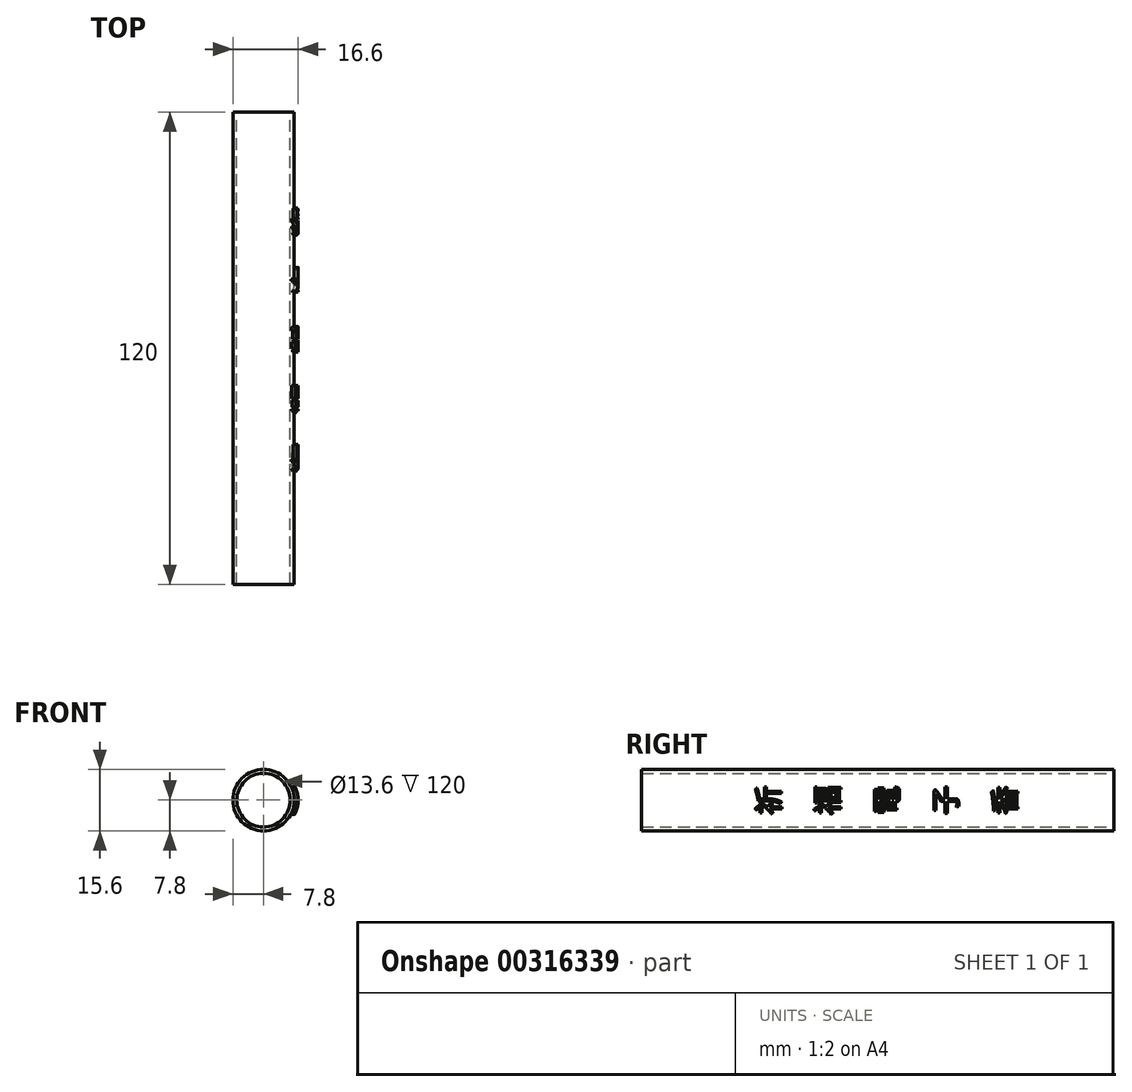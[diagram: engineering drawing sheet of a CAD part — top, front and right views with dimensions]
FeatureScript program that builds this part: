
annotation { "Feature Type Name" : "Feature", "Feature Type Description" : "" }
export const myFeature = defineFeature(function(context is Context, id is Id, definition is map)
    precondition{}
    {
        {
            var Q0;
            Q0=qCreatedBy(makeId("Front.planeOp"),FACE);
            var sketch = newSketch(context, id + "F0", { "sketchPlane" : qUnion([Q0])});
            skCircle(sketch, "E0", {"center": v(0, 0) * mm, "radius": 7.8 * mm});
            skSolve(sketch);
        }
        {
            var Q0;
            Q0=qSketchRegion(id+"F0",true);
            extrude(context, id + "F1", {"entities" : qUnion([Q0]), "depth" : 120 * mm});
        }
        {
            var Q0;
            Q0=makeQuery(id+"F1.opExtrude","CAP_FACE",FACE,{"disambiguationData":[OSD([sQuery(id+"F0.wireOp",EDGE,"E0")])],"isStart":true});
            var sketch = newSketch(context, id + "F2", { "sketchPlane" : qUnion([Q0])});
            skCircle(sketch, "E1", {"center": v(0, 0) * mm, "radius": 6.8 * mm});
            skSolve(sketch);
        }
        {
            var Q0;
            Q0=qSketchRegion(id+"F2",true);
            extrude(context, id + "F3", {"entities" : qUnion([Q0]), "operationType" : NewBodyOperationType.REMOVE, "oppositeDirection" : true, "depth" : 120 * mm});
        }
        {
            var Q0;
            Q0=qCreatedBy(makeId("Right.planeOp"),FACE);
            cPlane(context, id + "F4", {"entities" : qUnion([Q0]), "cplaneType" : CPlaneType.OFFSET, "offset" : 10 * mm, "width" : 150 * mm, "height" : 150 * mm});
        }
        {
            var Q0;
            Q0=qCreatedBy(id+"F4.planeOp",FACE);
            var sketch = newSketch(context, id + "F5", { "sketchPlane" : qUnion([Q0])});
            skText(sketch, "E2", { "text": "祈", "fontName": "NotoSansCJKtc-Regular.otf"});
            skText(sketch, "E3", { "text": "福", "fontName": "NotoSansCJKtc-Regular.otf"});
            skText(sketch, "E4", { "text": "電", "fontName": "NotoSansCJKtc-Regular.otf"});
            skText(sketch, "E5", { "text": "子", "fontName": "NotoSansCJKtc-Regular.otf"});
            skText(sketch, "E6", { "text": "香", "fontName": "NotoSansCJKtc-Regular.otf"});
            const initialGuessF5  = {"E2": [-0.085, -0.00375, 0, 1, 0.00534], "E3": [-0.07, -0.00375, 0, 1, 0.00543], "E4": [-0.055, -0.00375, 0, 1, 0.00532], "E5": [-0.04, -0.00375, 0, 1, 0.00537], "E6": [-0.025, -0.00375, 0, 1, 0.00536]};
            skSetInitialGuess(sketch, initialGuessF5);
            skSolve(sketch);
        }
        {
            var Q0;
            Q0=qSketchRegion(id+"F5",true);
            var Q1;
            Q1=makeQuery(id+"F1.opExtrude","SWEPT_FACE",FACE,{"disambiguationData":[OSD([sQuery(id+"F0.wireOp",EDGE,"E0")])]});
            extrude(context, id + "F6", {"entities" : qUnion([Q0]), "endBound" : BoundingType.UP_TO_SURFACE, "oppositeDirection" : true, "endBoundEntityFace" : qUnion([Q1]), "depth" : 2 * mm});
        }
        {
            var Q0;
            Q0=makeQuery(id+"F6.opExtrude","SWEPT_BODY",BODY,{"disambiguationData":[OSD([sQuery(id+"F5.wireOp",EDGE,"E2.sketch_text.stroke-0"),sQuery(id+"F5.wireOp",EDGE,"E2.sketch_text.stroke-1"),sQuery(id+"F5.wireOp",EDGE,"E2.sketch_text.stroke-2"),sQuery(id+"F5.wireOp",EDGE,"E2.sketch_text.stroke-3")])]});
            var Q1;
            Q1=makeQuery(id+"F6.opExtrude","SWEPT_BODY",BODY,{"disambiguationData":[OSD([sQuery(id+"F5.wireOp",EDGE,"E2.sketch_text.stroke-4"),sQuery(id+"F5.wireOp",EDGE,"E2.sketch_text.stroke-5"),sQuery(id+"F5.wireOp",EDGE,"E2.sketch_text.stroke-6"),sQuery(id+"F5.wireOp",EDGE,"E2.sketch_text.stroke-7"),sQuery(id+"F5.wireOp",EDGE,"E2.sketch_text.stroke-8"),sQuery(id+"F5.wireOp",EDGE,"E2.sketch_text.stroke-9"),sQuery(id+"F5.wireOp",EDGE,"E2.sketch_text.stroke-10"),sQuery(id+"F5.wireOp",EDGE,"E2.sketch_text.stroke-11"),sQuery(id+"F5.wireOp",EDGE,"E2.sketch_text.stroke-12"),sQuery(id+"F5.wireOp",EDGE,"E2.sketch_text.stroke-13"),sQuery(id+"F5.wireOp",EDGE,"E2.sketch_text.stroke-14"),sQuery(id+"F5.wireOp",EDGE,"E2.sketch_text.stroke-15"),sQuery(id+"F5.wireOp",EDGE,"E2.sketch_text.stroke-16"),sQuery(id+"F5.wireOp",EDGE,"E2.sketch_text.stroke-17"),sQuery(id+"F5.wireOp",EDGE,"E2.sketch_text.stroke-18")])]});
            var Q2;
            Q2=makeQuery(id+"F6.opExtrude","SWEPT_BODY",BODY,{"disambiguationData":[OSD([sQuery(id+"F5.wireOp",EDGE,"E2.sketch_text.stroke-19"),sQuery(id+"F5.wireOp",EDGE,"E2.sketch_text.stroke-20"),sQuery(id+"F5.wireOp",EDGE,"E2.sketch_text.stroke-21"),sQuery(id+"F5.wireOp",EDGE,"E2.sketch_text.stroke-22"),sQuery(id+"F5.wireOp",EDGE,"E2.sketch_text.stroke-23"),sQuery(id+"F5.wireOp",EDGE,"E2.sketch_text.stroke-24"),sQuery(id+"F5.wireOp",EDGE,"E2.sketch_text.stroke-25"),sQuery(id+"F5.wireOp",EDGE,"E2.sketch_text.stroke-26"),sQuery(id+"F5.wireOp",EDGE,"E2.sketch_text.stroke-27"),sQuery(id+"F5.wireOp",EDGE,"E2.sketch_text.stroke-28"),sQuery(id+"F5.wireOp",EDGE,"E2.sketch_text.stroke-29"),sQuery(id+"F5.wireOp",EDGE,"E2.sketch_text.stroke-30"),sQuery(id+"F5.wireOp",EDGE,"E2.sketch_text.stroke-31"),sQuery(id+"F5.wireOp",EDGE,"E2.sketch_text.stroke-32"),sQuery(id+"F5.wireOp",EDGE,"E2.sketch_text.stroke-33")])]});
            transform(context, id + "F7", {"entities" : qUnion([Q0, Q1, Q2]), "transformType" : TransformType.TRANSLATION_3D, "dx" : 1 * mm, "dy" : 0 * mm, "dz" : 0 * mm, "makeCopy" : true});
        }
        {
            var Q0;
            Q0=makeQuery(id+"F7.opPattern","COPY",BODY,{"derivedFrom":makeQuery(id+"F6.opExtrude","SWEPT_BODY",BODY,{"disambiguationData":[OSD([sQuery(id+"F5.wireOp",EDGE,"E2.sketch_text.stroke-19"),sQuery(id+"F5.wireOp",EDGE,"E2.sketch_text.stroke-20"),sQuery(id+"F5.wireOp",EDGE,"E2.sketch_text.stroke-21"),sQuery(id+"F5.wireOp",EDGE,"E2.sketch_text.stroke-22"),sQuery(id+"F5.wireOp",EDGE,"E2.sketch_text.stroke-23"),sQuery(id+"F5.wireOp",EDGE,"E2.sketch_text.stroke-24"),sQuery(id+"F5.wireOp",EDGE,"E2.sketch_text.stroke-25"),sQuery(id+"F5.wireOp",EDGE,"E2.sketch_text.stroke-26"),sQuery(id+"F5.wireOp",EDGE,"E2.sketch_text.stroke-27"),sQuery(id+"F5.wireOp",EDGE,"E2.sketch_text.stroke-28"),sQuery(id+"F5.wireOp",EDGE,"E2.sketch_text.stroke-29"),sQuery(id+"F5.wireOp",EDGE,"E2.sketch_text.stroke-30"),sQuery(id+"F5.wireOp",EDGE,"E2.sketch_text.stroke-31"),sQuery(id+"F5.wireOp",EDGE,"E2.sketch_text.stroke-32"),sQuery(id+"F5.wireOp",EDGE,"E2.sketch_text.stroke-33")])]}),"instanceName":"1"});
            var Q1;
            Q1=makeQuery(id+"F7.opPattern","COPY",BODY,{"derivedFrom":makeQuery(id+"F6.opExtrude","SWEPT_BODY",BODY,{"disambiguationData":[OSD([sQuery(id+"F5.wireOp",EDGE,"E2.sketch_text.stroke-4"),sQuery(id+"F5.wireOp",EDGE,"E2.sketch_text.stroke-5"),sQuery(id+"F5.wireOp",EDGE,"E2.sketch_text.stroke-6"),sQuery(id+"F5.wireOp",EDGE,"E2.sketch_text.stroke-7"),sQuery(id+"F5.wireOp",EDGE,"E2.sketch_text.stroke-8"),sQuery(id+"F5.wireOp",EDGE,"E2.sketch_text.stroke-9"),sQuery(id+"F5.wireOp",EDGE,"E2.sketch_text.stroke-10"),sQuery(id+"F5.wireOp",EDGE,"E2.sketch_text.stroke-11"),sQuery(id+"F5.wireOp",EDGE,"E2.sketch_text.stroke-12"),sQuery(id+"F5.wireOp",EDGE,"E2.sketch_text.stroke-13"),sQuery(id+"F5.wireOp",EDGE,"E2.sketch_text.stroke-14"),sQuery(id+"F5.wireOp",EDGE,"E2.sketch_text.stroke-15"),sQuery(id+"F5.wireOp",EDGE,"E2.sketch_text.stroke-16"),sQuery(id+"F5.wireOp",EDGE,"E2.sketch_text.stroke-17"),sQuery(id+"F5.wireOp",EDGE,"E2.sketch_text.stroke-18")])]}),"instanceName":"1"});
            var Q2;
            Q2=makeQuery(id+"F7.opPattern","COPY",BODY,{"derivedFrom":makeQuery(id+"F6.opExtrude","SWEPT_BODY",BODY,{"disambiguationData":[OSD([sQuery(id+"F5.wireOp",EDGE,"E2.sketch_text.stroke-0"),sQuery(id+"F5.wireOp",EDGE,"E2.sketch_text.stroke-1"),sQuery(id+"F5.wireOp",EDGE,"E2.sketch_text.stroke-2"),sQuery(id+"F5.wireOp",EDGE,"E2.sketch_text.stroke-3")])]}),"instanceName":"1"});
            var Q3;
            Q3=makeQuery(id+"F6.opExtrude","SWEPT_BODY",BODY,{"disambiguationData":[OSD([sQuery(id+"F5.wireOp",EDGE,"E2.sketch_text.stroke-0"),sQuery(id+"F5.wireOp",EDGE,"E2.sketch_text.stroke-1"),sQuery(id+"F5.wireOp",EDGE,"E2.sketch_text.stroke-2"),sQuery(id+"F5.wireOp",EDGE,"E2.sketch_text.stroke-3")])]});
            var Q4;
            Q4=makeQuery(id+"F6.opExtrude","SWEPT_BODY",BODY,{"disambiguationData":[OSD([sQuery(id+"F5.wireOp",EDGE,"E2.sketch_text.stroke-4"),sQuery(id+"F5.wireOp",EDGE,"E2.sketch_text.stroke-5"),sQuery(id+"F5.wireOp",EDGE,"E2.sketch_text.stroke-6"),sQuery(id+"F5.wireOp",EDGE,"E2.sketch_text.stroke-7"),sQuery(id+"F5.wireOp",EDGE,"E2.sketch_text.stroke-8"),sQuery(id+"F5.wireOp",EDGE,"E2.sketch_text.stroke-9"),sQuery(id+"F5.wireOp",EDGE,"E2.sketch_text.stroke-10"),sQuery(id+"F5.wireOp",EDGE,"E2.sketch_text.stroke-11"),sQuery(id+"F5.wireOp",EDGE,"E2.sketch_text.stroke-12"),sQuery(id+"F5.wireOp",EDGE,"E2.sketch_text.stroke-13"),sQuery(id+"F5.wireOp",EDGE,"E2.sketch_text.stroke-14"),sQuery(id+"F5.wireOp",EDGE,"E2.sketch_text.stroke-15"),sQuery(id+"F5.wireOp",EDGE,"E2.sketch_text.stroke-16"),sQuery(id+"F5.wireOp",EDGE,"E2.sketch_text.stroke-17"),sQuery(id+"F5.wireOp",EDGE,"E2.sketch_text.stroke-18")])]});
            var Q5;
            Q5=makeQuery(id+"F6.opExtrude","SWEPT_BODY",BODY,{"disambiguationData":[OSD([sQuery(id+"F5.wireOp",EDGE,"E2.sketch_text.stroke-19"),sQuery(id+"F5.wireOp",EDGE,"E2.sketch_text.stroke-20"),sQuery(id+"F5.wireOp",EDGE,"E2.sketch_text.stroke-21"),sQuery(id+"F5.wireOp",EDGE,"E2.sketch_text.stroke-22"),sQuery(id+"F5.wireOp",EDGE,"E2.sketch_text.stroke-23"),sQuery(id+"F5.wireOp",EDGE,"E2.sketch_text.stroke-24"),sQuery(id+"F5.wireOp",EDGE,"E2.sketch_text.stroke-25"),sQuery(id+"F5.wireOp",EDGE,"E2.sketch_text.stroke-26"),sQuery(id+"F5.wireOp",EDGE,"E2.sketch_text.stroke-27"),sQuery(id+"F5.wireOp",EDGE,"E2.sketch_text.stroke-28"),sQuery(id+"F5.wireOp",EDGE,"E2.sketch_text.stroke-29"),sQuery(id+"F5.wireOp",EDGE,"E2.sketch_text.stroke-30"),sQuery(id+"F5.wireOp",EDGE,"E2.sketch_text.stroke-31"),sQuery(id+"F5.wireOp",EDGE,"E2.sketch_text.stroke-32"),sQuery(id+"F5.wireOp",EDGE,"E2.sketch_text.stroke-33")])]});
            booleanBodies(context, id + "F8", {"operationType" : BooleanOperationType.SUBTRACTION, "tools" : qUnion([Q0, Q1, Q2]), "targets" : qUnion([Q3, Q4, Q5])});
        }
        {
            var Q0;
            Q0=makeQuery(id+"F6.opExtrude","SWEPT_BODY",BODY,{"disambiguationData":[OSD([sQuery(id+"F5.wireOp",EDGE,"E3.sketch_text.stroke-0"),sQuery(id+"F5.wireOp",EDGE,"E3.sketch_text.stroke-1"),sQuery(id+"F5.wireOp",EDGE,"E3.sketch_text.stroke-2"),sQuery(id+"F5.wireOp",EDGE,"E3.sketch_text.stroke-3")])]});
            var Q1;
            Q1=makeQuery(id+"F6.opExtrude","SWEPT_BODY",BODY,{"disambiguationData":[OSD([sQuery(id+"F5.wireOp",EDGE,"E3.sketch_text.stroke-4"),sQuery(id+"F5.wireOp",EDGE,"E3.sketch_text.stroke-5"),sQuery(id+"F5.wireOp",EDGE,"E3.sketch_text.stroke-6"),sQuery(id+"F5.wireOp",EDGE,"E3.sketch_text.stroke-7"),sQuery(id+"F5.wireOp",EDGE,"E3.sketch_text.stroke-8"),sQuery(id+"F5.wireOp",EDGE,"E3.sketch_text.stroke-9"),sQuery(id+"F5.wireOp",EDGE,"E3.sketch_text.stroke-10"),sQuery(id+"F5.wireOp",EDGE,"E3.sketch_text.stroke-11"),sQuery(id+"F5.wireOp",EDGE,"E3.sketch_text.stroke-12"),sQuery(id+"F5.wireOp",EDGE,"E3.sketch_text.stroke-13"),sQuery(id+"F5.wireOp",EDGE,"E3.sketch_text.stroke-14"),sQuery(id+"F5.wireOp",EDGE,"E3.sketch_text.stroke-15"),sQuery(id+"F5.wireOp",EDGE,"E3.sketch_text.stroke-16"),sQuery(id+"F5.wireOp",EDGE,"E3.sketch_text.stroke-17"),sQuery(id+"F5.wireOp",EDGE,"E3.sketch_text.stroke-18"),sQuery(id+"F5.wireOp",EDGE,"E3.sketch_text.stroke-19"),sQuery(id+"F5.wireOp",EDGE,"E3.sketch_text.stroke-20"),sQuery(id+"F5.wireOp",EDGE,"E3.sketch_text.stroke-21"),sQuery(id+"F5.wireOp",EDGE,"E3.sketch_text.stroke-22"),sQuery(id+"F5.wireOp",EDGE,"E3.sketch_text.stroke-23"),sQuery(id+"F5.wireOp",EDGE,"E3.sketch_text.stroke-24"),sQuery(id+"F5.wireOp",EDGE,"E3.sketch_text.stroke-25"),sQuery(id+"F5.wireOp",EDGE,"E3.sketch_text.stroke-26"),sQuery(id+"F5.wireOp",EDGE,"E3.sketch_text.stroke-27"),sQuery(id+"F5.wireOp",EDGE,"E3.sketch_text.stroke-28"),sQuery(id+"F5.wireOp",EDGE,"E3.sketch_text.stroke-29"),sQuery(id+"F5.wireOp",EDGE,"E3.sketch_text.stroke-30"),sQuery(id+"F5.wireOp",EDGE,"E3.sketch_text.stroke-31"),sQuery(id+"F5.wireOp",EDGE,"E3.sketch_text.stroke-32"),sQuery(id+"F5.wireOp",EDGE,"E3.sketch_text.stroke-33"),sQuery(id+"F5.wireOp",EDGE,"E3.sketch_text.stroke-34"),sQuery(id+"F5.wireOp",EDGE,"E3.sketch_text.stroke-35"),sQuery(id+"F5.wireOp",EDGE,"E3.sketch_text.stroke-36"),sQuery(id+"F5.wireOp",EDGE,"E3.sketch_text.stroke-37"),sQuery(id+"F5.wireOp",EDGE,"E3.sketch_text.stroke-38"),sQuery(id+"F5.wireOp",EDGE,"E3.sketch_text.stroke-39"),sQuery(id+"F5.wireOp",EDGE,"E3.sketch_text.stroke-40"),sQuery(id+"F5.wireOp",EDGE,"E3.sketch_text.stroke-41"),sQuery(id+"F5.wireOp",EDGE,"E3.sketch_text.stroke-42"),sQuery(id+"F5.wireOp",EDGE,"E3.sketch_text.stroke-43")])]});
            var Q2;
            Q2=makeQuery(id+"F6.opExtrude","SWEPT_BODY",BODY,{"disambiguationData":[OSD([sQuery(id+"F5.wireOp",EDGE,"E3.sketch_text.stroke-44"),sQuery(id+"F5.wireOp",EDGE,"E3.sketch_text.stroke-45"),sQuery(id+"F5.wireOp",EDGE,"E3.sketch_text.stroke-46"),sQuery(id+"F5.wireOp",EDGE,"E3.sketch_text.stroke-47"),sQuery(id+"F5.wireOp",EDGE,"E3.sketch_text.stroke-48"),sQuery(id+"F5.wireOp",EDGE,"E3.sketch_text.stroke-49"),sQuery(id+"F5.wireOp",EDGE,"E3.sketch_text.stroke-50"),sQuery(id+"F5.wireOp",EDGE,"E3.sketch_text.stroke-51")])]});
            var Q3;
            Q3=makeQuery(id+"F6.opExtrude","SWEPT_BODY",BODY,{"disambiguationData":[OSD([sQuery(id+"F5.wireOp",EDGE,"E3.sketch_text.stroke-52"),sQuery(id+"F5.wireOp",EDGE,"E3.sketch_text.stroke-53"),sQuery(id+"F5.wireOp",EDGE,"E3.sketch_text.stroke-54"),sQuery(id+"F5.wireOp",EDGE,"E3.sketch_text.stroke-55")])]});
            transform(context, id + "F9", {"entities" : qUnion([Q0, Q1, Q2, Q3]), "transformType" : TransformType.TRANSLATION_3D, "dx" : 1 * mm, "dy" : 0 * mm, "dz" : 0 * mm, "makeCopy" : true});
        }
        {
            var Q0;
            Q0=makeQuery(id+"F9.opPattern","COPY",BODY,{"derivedFrom":makeQuery(id+"F6.opExtrude","SWEPT_BODY",BODY,{"disambiguationData":[OSD([sQuery(id+"F5.wireOp",EDGE,"E3.sketch_text.stroke-52"),sQuery(id+"F5.wireOp",EDGE,"E3.sketch_text.stroke-53"),sQuery(id+"F5.wireOp",EDGE,"E3.sketch_text.stroke-54"),sQuery(id+"F5.wireOp",EDGE,"E3.sketch_text.stroke-55")])]}),"instanceName":"1"});
            var Q1;
            Q1=makeQuery(id+"F9.opPattern","COPY",BODY,{"derivedFrom":makeQuery(id+"F6.opExtrude","SWEPT_BODY",BODY,{"disambiguationData":[OSD([sQuery(id+"F5.wireOp",EDGE,"E3.sketch_text.stroke-44"),sQuery(id+"F5.wireOp",EDGE,"E3.sketch_text.stroke-45"),sQuery(id+"F5.wireOp",EDGE,"E3.sketch_text.stroke-46"),sQuery(id+"F5.wireOp",EDGE,"E3.sketch_text.stroke-47"),sQuery(id+"F5.wireOp",EDGE,"E3.sketch_text.stroke-48"),sQuery(id+"F5.wireOp",EDGE,"E3.sketch_text.stroke-49"),sQuery(id+"F5.wireOp",EDGE,"E3.sketch_text.stroke-50"),sQuery(id+"F5.wireOp",EDGE,"E3.sketch_text.stroke-51")])]}),"instanceName":"1"});
            var Q2;
            Q2=makeQuery(id+"F9.opPattern","COPY",BODY,{"derivedFrom":makeQuery(id+"F6.opExtrude","SWEPT_BODY",BODY,{"disambiguationData":[OSD([sQuery(id+"F5.wireOp",EDGE,"E3.sketch_text.stroke-4"),sQuery(id+"F5.wireOp",EDGE,"E3.sketch_text.stroke-5"),sQuery(id+"F5.wireOp",EDGE,"E3.sketch_text.stroke-6"),sQuery(id+"F5.wireOp",EDGE,"E3.sketch_text.stroke-7"),sQuery(id+"F5.wireOp",EDGE,"E3.sketch_text.stroke-8"),sQuery(id+"F5.wireOp",EDGE,"E3.sketch_text.stroke-9"),sQuery(id+"F5.wireOp",EDGE,"E3.sketch_text.stroke-10"),sQuery(id+"F5.wireOp",EDGE,"E3.sketch_text.stroke-11"),sQuery(id+"F5.wireOp",EDGE,"E3.sketch_text.stroke-12"),sQuery(id+"F5.wireOp",EDGE,"E3.sketch_text.stroke-13"),sQuery(id+"F5.wireOp",EDGE,"E3.sketch_text.stroke-14"),sQuery(id+"F5.wireOp",EDGE,"E3.sketch_text.stroke-15"),sQuery(id+"F5.wireOp",EDGE,"E3.sketch_text.stroke-16"),sQuery(id+"F5.wireOp",EDGE,"E3.sketch_text.stroke-17"),sQuery(id+"F5.wireOp",EDGE,"E3.sketch_text.stroke-18"),sQuery(id+"F5.wireOp",EDGE,"E3.sketch_text.stroke-19"),sQuery(id+"F5.wireOp",EDGE,"E3.sketch_text.stroke-20"),sQuery(id+"F5.wireOp",EDGE,"E3.sketch_text.stroke-21"),sQuery(id+"F5.wireOp",EDGE,"E3.sketch_text.stroke-22"),sQuery(id+"F5.wireOp",EDGE,"E3.sketch_text.stroke-23"),sQuery(id+"F5.wireOp",EDGE,"E3.sketch_text.stroke-24"),sQuery(id+"F5.wireOp",EDGE,"E3.sketch_text.stroke-25"),sQuery(id+"F5.wireOp",EDGE,"E3.sketch_text.stroke-26"),sQuery(id+"F5.wireOp",EDGE,"E3.sketch_text.stroke-27"),sQuery(id+"F5.wireOp",EDGE,"E3.sketch_text.stroke-28"),sQuery(id+"F5.wireOp",EDGE,"E3.sketch_text.stroke-29"),sQuery(id+"F5.wireOp",EDGE,"E3.sketch_text.stroke-30"),sQuery(id+"F5.wireOp",EDGE,"E3.sketch_text.stroke-31"),sQuery(id+"F5.wireOp",EDGE,"E3.sketch_text.stroke-32"),sQuery(id+"F5.wireOp",EDGE,"E3.sketch_text.stroke-33"),sQuery(id+"F5.wireOp",EDGE,"E3.sketch_text.stroke-34"),sQuery(id+"F5.wireOp",EDGE,"E3.sketch_text.stroke-35"),sQuery(id+"F5.wireOp",EDGE,"E3.sketch_text.stroke-36"),sQuery(id+"F5.wireOp",EDGE,"E3.sketch_text.stroke-37"),sQuery(id+"F5.wireOp",EDGE,"E3.sketch_text.stroke-38"),sQuery(id+"F5.wireOp",EDGE,"E3.sketch_text.stroke-39"),sQuery(id+"F5.wireOp",EDGE,"E3.sketch_text.stroke-40"),sQuery(id+"F5.wireOp",EDGE,"E3.sketch_text.stroke-41"),sQuery(id+"F5.wireOp",EDGE,"E3.sketch_text.stroke-42"),sQuery(id+"F5.wireOp",EDGE,"E3.sketch_text.stroke-43")])]}),"instanceName":"1"});
            var Q3;
            Q3=makeQuery(id+"F9.opPattern","COPY",BODY,{"derivedFrom":makeQuery(id+"F6.opExtrude","SWEPT_BODY",BODY,{"disambiguationData":[OSD([sQuery(id+"F5.wireOp",EDGE,"E3.sketch_text.stroke-0"),sQuery(id+"F5.wireOp",EDGE,"E3.sketch_text.stroke-1"),sQuery(id+"F5.wireOp",EDGE,"E3.sketch_text.stroke-2"),sQuery(id+"F5.wireOp",EDGE,"E3.sketch_text.stroke-3")])]}),"instanceName":"1"});
            var Q4;
            Q4=makeQuery(id+"F6.opExtrude","SWEPT_BODY",BODY,{"disambiguationData":[OSD([sQuery(id+"F5.wireOp",EDGE,"E3.sketch_text.stroke-0"),sQuery(id+"F5.wireOp",EDGE,"E3.sketch_text.stroke-1"),sQuery(id+"F5.wireOp",EDGE,"E3.sketch_text.stroke-2"),sQuery(id+"F5.wireOp",EDGE,"E3.sketch_text.stroke-3")])]});
            var Q5;
            Q5=makeQuery(id+"F6.opExtrude","SWEPT_BODY",BODY,{"disambiguationData":[OSD([sQuery(id+"F5.wireOp",EDGE,"E3.sketch_text.stroke-4"),sQuery(id+"F5.wireOp",EDGE,"E3.sketch_text.stroke-5"),sQuery(id+"F5.wireOp",EDGE,"E3.sketch_text.stroke-6"),sQuery(id+"F5.wireOp",EDGE,"E3.sketch_text.stroke-7"),sQuery(id+"F5.wireOp",EDGE,"E3.sketch_text.stroke-8"),sQuery(id+"F5.wireOp",EDGE,"E3.sketch_text.stroke-9"),sQuery(id+"F5.wireOp",EDGE,"E3.sketch_text.stroke-10"),sQuery(id+"F5.wireOp",EDGE,"E3.sketch_text.stroke-11"),sQuery(id+"F5.wireOp",EDGE,"E3.sketch_text.stroke-12"),sQuery(id+"F5.wireOp",EDGE,"E3.sketch_text.stroke-13"),sQuery(id+"F5.wireOp",EDGE,"E3.sketch_text.stroke-14"),sQuery(id+"F5.wireOp",EDGE,"E3.sketch_text.stroke-15"),sQuery(id+"F5.wireOp",EDGE,"E3.sketch_text.stroke-16"),sQuery(id+"F5.wireOp",EDGE,"E3.sketch_text.stroke-17"),sQuery(id+"F5.wireOp",EDGE,"E3.sketch_text.stroke-18"),sQuery(id+"F5.wireOp",EDGE,"E3.sketch_text.stroke-19"),sQuery(id+"F5.wireOp",EDGE,"E3.sketch_text.stroke-20"),sQuery(id+"F5.wireOp",EDGE,"E3.sketch_text.stroke-21"),sQuery(id+"F5.wireOp",EDGE,"E3.sketch_text.stroke-22"),sQuery(id+"F5.wireOp",EDGE,"E3.sketch_text.stroke-23"),sQuery(id+"F5.wireOp",EDGE,"E3.sketch_text.stroke-24"),sQuery(id+"F5.wireOp",EDGE,"E3.sketch_text.stroke-25"),sQuery(id+"F5.wireOp",EDGE,"E3.sketch_text.stroke-26"),sQuery(id+"F5.wireOp",EDGE,"E3.sketch_text.stroke-27"),sQuery(id+"F5.wireOp",EDGE,"E3.sketch_text.stroke-28"),sQuery(id+"F5.wireOp",EDGE,"E3.sketch_text.stroke-29"),sQuery(id+"F5.wireOp",EDGE,"E3.sketch_text.stroke-30"),sQuery(id+"F5.wireOp",EDGE,"E3.sketch_text.stroke-31"),sQuery(id+"F5.wireOp",EDGE,"E3.sketch_text.stroke-32"),sQuery(id+"F5.wireOp",EDGE,"E3.sketch_text.stroke-33"),sQuery(id+"F5.wireOp",EDGE,"E3.sketch_text.stroke-34"),sQuery(id+"F5.wireOp",EDGE,"E3.sketch_text.stroke-35"),sQuery(id+"F5.wireOp",EDGE,"E3.sketch_text.stroke-36"),sQuery(id+"F5.wireOp",EDGE,"E3.sketch_text.stroke-37"),sQuery(id+"F5.wireOp",EDGE,"E3.sketch_text.stroke-38"),sQuery(id+"F5.wireOp",EDGE,"E3.sketch_text.stroke-39"),sQuery(id+"F5.wireOp",EDGE,"E3.sketch_text.stroke-40"),sQuery(id+"F5.wireOp",EDGE,"E3.sketch_text.stroke-41"),sQuery(id+"F5.wireOp",EDGE,"E3.sketch_text.stroke-42"),sQuery(id+"F5.wireOp",EDGE,"E3.sketch_text.stroke-43")])]});
            var Q6;
            Q6=makeQuery(id+"F6.opExtrude","SWEPT_BODY",BODY,{"disambiguationData":[OSD([sQuery(id+"F5.wireOp",EDGE,"E3.sketch_text.stroke-44"),sQuery(id+"F5.wireOp",EDGE,"E3.sketch_text.stroke-45"),sQuery(id+"F5.wireOp",EDGE,"E3.sketch_text.stroke-46"),sQuery(id+"F5.wireOp",EDGE,"E3.sketch_text.stroke-47"),sQuery(id+"F5.wireOp",EDGE,"E3.sketch_text.stroke-48"),sQuery(id+"F5.wireOp",EDGE,"E3.sketch_text.stroke-49"),sQuery(id+"F5.wireOp",EDGE,"E3.sketch_text.stroke-50"),sQuery(id+"F5.wireOp",EDGE,"E3.sketch_text.stroke-51")])]});
            var Q7;
            Q7=makeQuery(id+"F6.opExtrude","SWEPT_BODY",BODY,{"disambiguationData":[OSD([sQuery(id+"F5.wireOp",EDGE,"E3.sketch_text.stroke-52"),sQuery(id+"F5.wireOp",EDGE,"E3.sketch_text.stroke-53"),sQuery(id+"F5.wireOp",EDGE,"E3.sketch_text.stroke-54"),sQuery(id+"F5.wireOp",EDGE,"E3.sketch_text.stroke-55")])]});
            booleanBodies(context, id + "F10", {"operationType" : BooleanOperationType.SUBTRACTION, "tools" : qUnion([Q0, Q1, Q2, Q3]), "targets" : qUnion([Q4, Q5, Q6, Q7])});
        }
        {
            var Q0;
            Q0=makeQuery(id+"F6.opExtrude","SWEPT_BODY",BODY,{"disambiguationData":[OSD([sQuery(id+"F5.wireOp",EDGE,"E4.sketch_text.stroke-0"),sQuery(id+"F5.wireOp",EDGE,"E4.sketch_text.stroke-1"),sQuery(id+"F5.wireOp",EDGE,"E4.sketch_text.stroke-2"),sQuery(id+"F5.wireOp",EDGE,"E4.sketch_text.stroke-3"),sQuery(id+"F5.wireOp",EDGE,"E4.sketch_text.stroke-4"),sQuery(id+"F5.wireOp",EDGE,"E4.sketch_text.stroke-5"),sQuery(id+"F5.wireOp",EDGE,"E4.sketch_text.stroke-6"),sQuery(id+"F5.wireOp",EDGE,"E4.sketch_text.stroke-7"),sQuery(id+"F5.wireOp",EDGE,"E4.sketch_text.stroke-8"),sQuery(id+"F5.wireOp",EDGE,"E4.sketch_text.stroke-9"),sQuery(id+"F5.wireOp",EDGE,"E4.sketch_text.stroke-10"),sQuery(id+"F5.wireOp",EDGE,"E4.sketch_text.stroke-11"),sQuery(id+"F5.wireOp",EDGE,"E4.sketch_text.stroke-12"),sQuery(id+"F5.wireOp",EDGE,"E4.sketch_text.stroke-13"),sQuery(id+"F5.wireOp",EDGE,"E4.sketch_text.stroke-14"),sQuery(id+"F5.wireOp",EDGE,"E4.sketch_text.stroke-15"),sQuery(id+"F5.wireOp",EDGE,"E4.sketch_text.stroke-16"),sQuery(id+"F5.wireOp",EDGE,"E4.sketch_text.stroke-17"),sQuery(id+"F5.wireOp",EDGE,"E4.sketch_text.stroke-18"),sQuery(id+"F5.wireOp",EDGE,"E4.sketch_text.stroke-19")])]});
            var Q1;
            Q1=makeQuery(id+"F6.opExtrude","SWEPT_BODY",BODY,{"disambiguationData":[OSD([sQuery(id+"F5.wireOp",EDGE,"E4.sketch_text.stroke-20"),sQuery(id+"F5.wireOp",EDGE,"E4.sketch_text.stroke-21"),sQuery(id+"F5.wireOp",EDGE,"E4.sketch_text.stroke-22"),sQuery(id+"F5.wireOp",EDGE,"E4.sketch_text.stroke-23")])]});
            var Q2;
            Q2=makeQuery(id+"F6.opExtrude","SWEPT_BODY",BODY,{"disambiguationData":[OSD([sQuery(id+"F5.wireOp",EDGE,"E4.sketch_text.stroke-24"),sQuery(id+"F5.wireOp",EDGE,"E4.sketch_text.stroke-25"),sQuery(id+"F5.wireOp",EDGE,"E4.sketch_text.stroke-26"),sQuery(id+"F5.wireOp",EDGE,"E4.sketch_text.stroke-27")])]});
            var Q3;
            Q3=makeQuery(id+"F6.opExtrude","SWEPT_BODY",BODY,{"disambiguationData":[OSD([sQuery(id+"F5.wireOp",EDGE,"E4.sketch_text.stroke-28"),sQuery(id+"F5.wireOp",EDGE,"E4.sketch_text.stroke-29"),sQuery(id+"F5.wireOp",EDGE,"E4.sketch_text.stroke-30"),sQuery(id+"F5.wireOp",EDGE,"E4.sketch_text.stroke-31")])]});
            var Q4;
            Q4=makeQuery(id+"F6.opExtrude","SWEPT_BODY",BODY,{"disambiguationData":[OSD([sQuery(id+"F5.wireOp",EDGE,"E4.sketch_text.stroke-32"),sQuery(id+"F5.wireOp",EDGE,"E4.sketch_text.stroke-33"),sQuery(id+"F5.wireOp",EDGE,"E4.sketch_text.stroke-34"),sQuery(id+"F5.wireOp",EDGE,"E4.sketch_text.stroke-35")])]});
            var Q5;
            Q5=makeQuery(id+"F6.opExtrude","SWEPT_BODY",BODY,{"disambiguationData":[OSD([sQuery(id+"F5.wireOp",EDGE,"E4.sketch_text.stroke-36"),sQuery(id+"F5.wireOp",EDGE,"E4.sketch_text.stroke-37"),sQuery(id+"F5.wireOp",EDGE,"E4.sketch_text.stroke-38"),sQuery(id+"F5.wireOp",EDGE,"E4.sketch_text.stroke-39"),sQuery(id+"F5.wireOp",EDGE,"E4.sketch_text.stroke-40"),sQuery(id+"F5.wireOp",EDGE,"E4.sketch_text.stroke-41"),sQuery(id+"F5.wireOp",EDGE,"E4.sketch_text.stroke-42"),sQuery(id+"F5.wireOp",EDGE,"E4.sketch_text.stroke-43"),sQuery(id+"F5.wireOp",EDGE,"E4.sketch_text.stroke-44"),sQuery(id+"F5.wireOp",EDGE,"E4.sketch_text.stroke-45"),sQuery(id+"F5.wireOp",EDGE,"E4.sketch_text.stroke-46"),sQuery(id+"F5.wireOp",EDGE,"E4.sketch_text.stroke-47"),sQuery(id+"F5.wireOp",EDGE,"E4.sketch_text.stroke-48"),sQuery(id+"F5.wireOp",EDGE,"E4.sketch_text.stroke-49"),sQuery(id+"F5.wireOp",EDGE,"E4.sketch_text.stroke-50"),sQuery(id+"F5.wireOp",EDGE,"E4.sketch_text.stroke-51"),sQuery(id+"F5.wireOp",EDGE,"E4.sketch_text.stroke-52"),sQuery(id+"F5.wireOp",EDGE,"E4.sketch_text.stroke-53"),sQuery(id+"F5.wireOp",EDGE,"E4.sketch_text.stroke-54"),sQuery(id+"F5.wireOp",EDGE,"E4.sketch_text.stroke-55"),sQuery(id+"F5.wireOp",EDGE,"E4.sketch_text.stroke-56"),sQuery(id+"F5.wireOp",EDGE,"E4.sketch_text.stroke-57"),sQuery(id+"F5.wireOp",EDGE,"E4.sketch_text.stroke-58"),sQuery(id+"F5.wireOp",EDGE,"E4.sketch_text.stroke-59"),sQuery(id+"F5.wireOp",EDGE,"E4.sketch_text.stroke-60"),sQuery(id+"F5.wireOp",EDGE,"E4.sketch_text.stroke-61"),sQuery(id+"F5.wireOp",EDGE,"E4.sketch_text.stroke-62"),sQuery(id+"F5.wireOp",EDGE,"E4.sketch_text.stroke-63"),sQuery(id+"F5.wireOp",EDGE,"E4.sketch_text.stroke-64"),sQuery(id+"F5.wireOp",EDGE,"E4.sketch_text.stroke-65"),sQuery(id+"F5.wireOp",EDGE,"E4.sketch_text.stroke-66"),sQuery(id+"F5.wireOp",EDGE,"E4.sketch_text.stroke-67")])]});
            transform(context, id + "F11", {"entities" : qUnion([Q0, Q1, Q2, Q3, Q4, Q5]), "transformType" : TransformType.TRANSLATION_3D, "dx" : 1 * mm, "dy" : 0 * mm, "dz" : 0 * mm, "makeCopy" : true});
        }
        {
            var Q0;
            Q0=makeQuery(id+"F11.opPattern","COPY",BODY,{"derivedFrom":makeQuery(id+"F6.opExtrude","SWEPT_BODY",BODY,{"disambiguationData":[OSD([sQuery(id+"F5.wireOp",EDGE,"E4.sketch_text.stroke-36"),sQuery(id+"F5.wireOp",EDGE,"E4.sketch_text.stroke-37"),sQuery(id+"F5.wireOp",EDGE,"E4.sketch_text.stroke-38"),sQuery(id+"F5.wireOp",EDGE,"E4.sketch_text.stroke-39"),sQuery(id+"F5.wireOp",EDGE,"E4.sketch_text.stroke-40"),sQuery(id+"F5.wireOp",EDGE,"E4.sketch_text.stroke-41"),sQuery(id+"F5.wireOp",EDGE,"E4.sketch_text.stroke-42"),sQuery(id+"F5.wireOp",EDGE,"E4.sketch_text.stroke-43"),sQuery(id+"F5.wireOp",EDGE,"E4.sketch_text.stroke-44"),sQuery(id+"F5.wireOp",EDGE,"E4.sketch_text.stroke-45"),sQuery(id+"F5.wireOp",EDGE,"E4.sketch_text.stroke-46"),sQuery(id+"F5.wireOp",EDGE,"E4.sketch_text.stroke-47"),sQuery(id+"F5.wireOp",EDGE,"E4.sketch_text.stroke-48"),sQuery(id+"F5.wireOp",EDGE,"E4.sketch_text.stroke-49"),sQuery(id+"F5.wireOp",EDGE,"E4.sketch_text.stroke-50"),sQuery(id+"F5.wireOp",EDGE,"E4.sketch_text.stroke-51"),sQuery(id+"F5.wireOp",EDGE,"E4.sketch_text.stroke-52"),sQuery(id+"F5.wireOp",EDGE,"E4.sketch_text.stroke-53"),sQuery(id+"F5.wireOp",EDGE,"E4.sketch_text.stroke-54"),sQuery(id+"F5.wireOp",EDGE,"E4.sketch_text.stroke-55"),sQuery(id+"F5.wireOp",EDGE,"E4.sketch_text.stroke-56"),sQuery(id+"F5.wireOp",EDGE,"E4.sketch_text.stroke-57"),sQuery(id+"F5.wireOp",EDGE,"E4.sketch_text.stroke-58"),sQuery(id+"F5.wireOp",EDGE,"E4.sketch_text.stroke-59"),sQuery(id+"F5.wireOp",EDGE,"E4.sketch_text.stroke-60"),sQuery(id+"F5.wireOp",EDGE,"E4.sketch_text.stroke-61"),sQuery(id+"F5.wireOp",EDGE,"E4.sketch_text.stroke-62"),sQuery(id+"F5.wireOp",EDGE,"E4.sketch_text.stroke-63"),sQuery(id+"F5.wireOp",EDGE,"E4.sketch_text.stroke-64"),sQuery(id+"F5.wireOp",EDGE,"E4.sketch_text.stroke-65"),sQuery(id+"F5.wireOp",EDGE,"E4.sketch_text.stroke-66"),sQuery(id+"F5.wireOp",EDGE,"E4.sketch_text.stroke-67")])]}),"instanceName":"1"});
            var Q1;
            Q1=makeQuery(id+"F11.opPattern","COPY",BODY,{"derivedFrom":makeQuery(id+"F6.opExtrude","SWEPT_BODY",BODY,{"disambiguationData":[OSD([sQuery(id+"F5.wireOp",EDGE,"E4.sketch_text.stroke-32"),sQuery(id+"F5.wireOp",EDGE,"E4.sketch_text.stroke-33"),sQuery(id+"F5.wireOp",EDGE,"E4.sketch_text.stroke-34"),sQuery(id+"F5.wireOp",EDGE,"E4.sketch_text.stroke-35")])]}),"instanceName":"1"});
            var Q2;
            Q2=makeQuery(id+"F11.opPattern","COPY",BODY,{"derivedFrom":makeQuery(id+"F6.opExtrude","SWEPT_BODY",BODY,{"disambiguationData":[OSD([sQuery(id+"F5.wireOp",EDGE,"E4.sketch_text.stroke-28"),sQuery(id+"F5.wireOp",EDGE,"E4.sketch_text.stroke-29"),sQuery(id+"F5.wireOp",EDGE,"E4.sketch_text.stroke-30"),sQuery(id+"F5.wireOp",EDGE,"E4.sketch_text.stroke-31")])]}),"instanceName":"1"});
            var Q3;
            Q3=makeQuery(id+"F11.opPattern","COPY",BODY,{"derivedFrom":makeQuery(id+"F6.opExtrude","SWEPT_BODY",BODY,{"disambiguationData":[OSD([sQuery(id+"F5.wireOp",EDGE,"E4.sketch_text.stroke-24"),sQuery(id+"F5.wireOp",EDGE,"E4.sketch_text.stroke-25"),sQuery(id+"F5.wireOp",EDGE,"E4.sketch_text.stroke-26"),sQuery(id+"F5.wireOp",EDGE,"E4.sketch_text.stroke-27")])]}),"instanceName":"1"});
            var Q4;
            Q4=makeQuery(id+"F11.opPattern","COPY",BODY,{"derivedFrom":makeQuery(id+"F6.opExtrude","SWEPT_BODY",BODY,{"disambiguationData":[OSD([sQuery(id+"F5.wireOp",EDGE,"E4.sketch_text.stroke-20"),sQuery(id+"F5.wireOp",EDGE,"E4.sketch_text.stroke-21"),sQuery(id+"F5.wireOp",EDGE,"E4.sketch_text.stroke-22"),sQuery(id+"F5.wireOp",EDGE,"E4.sketch_text.stroke-23")])]}),"instanceName":"1"});
            var Q5;
            Q5=makeQuery(id+"F11.opPattern","COPY",BODY,{"derivedFrom":makeQuery(id+"F6.opExtrude","SWEPT_BODY",BODY,{"disambiguationData":[OSD([sQuery(id+"F5.wireOp",EDGE,"E4.sketch_text.stroke-0"),sQuery(id+"F5.wireOp",EDGE,"E4.sketch_text.stroke-1"),sQuery(id+"F5.wireOp",EDGE,"E4.sketch_text.stroke-2"),sQuery(id+"F5.wireOp",EDGE,"E4.sketch_text.stroke-3"),sQuery(id+"F5.wireOp",EDGE,"E4.sketch_text.stroke-4"),sQuery(id+"F5.wireOp",EDGE,"E4.sketch_text.stroke-5"),sQuery(id+"F5.wireOp",EDGE,"E4.sketch_text.stroke-6"),sQuery(id+"F5.wireOp",EDGE,"E4.sketch_text.stroke-7"),sQuery(id+"F5.wireOp",EDGE,"E4.sketch_text.stroke-8"),sQuery(id+"F5.wireOp",EDGE,"E4.sketch_text.stroke-9"),sQuery(id+"F5.wireOp",EDGE,"E4.sketch_text.stroke-10"),sQuery(id+"F5.wireOp",EDGE,"E4.sketch_text.stroke-11"),sQuery(id+"F5.wireOp",EDGE,"E4.sketch_text.stroke-12"),sQuery(id+"F5.wireOp",EDGE,"E4.sketch_text.stroke-13"),sQuery(id+"F5.wireOp",EDGE,"E4.sketch_text.stroke-14"),sQuery(id+"F5.wireOp",EDGE,"E4.sketch_text.stroke-15"),sQuery(id+"F5.wireOp",EDGE,"E4.sketch_text.stroke-16"),sQuery(id+"F5.wireOp",EDGE,"E4.sketch_text.stroke-17"),sQuery(id+"F5.wireOp",EDGE,"E4.sketch_text.stroke-18"),sQuery(id+"F5.wireOp",EDGE,"E4.sketch_text.stroke-19")])]}),"instanceName":"1"});
            var Q6;
            Q6=makeQuery(id+"F6.opExtrude","SWEPT_BODY",BODY,{"disambiguationData":[OSD([sQuery(id+"F5.wireOp",EDGE,"E4.sketch_text.stroke-0"),sQuery(id+"F5.wireOp",EDGE,"E4.sketch_text.stroke-1"),sQuery(id+"F5.wireOp",EDGE,"E4.sketch_text.stroke-2"),sQuery(id+"F5.wireOp",EDGE,"E4.sketch_text.stroke-3"),sQuery(id+"F5.wireOp",EDGE,"E4.sketch_text.stroke-4"),sQuery(id+"F5.wireOp",EDGE,"E4.sketch_text.stroke-5"),sQuery(id+"F5.wireOp",EDGE,"E4.sketch_text.stroke-6"),sQuery(id+"F5.wireOp",EDGE,"E4.sketch_text.stroke-7"),sQuery(id+"F5.wireOp",EDGE,"E4.sketch_text.stroke-8"),sQuery(id+"F5.wireOp",EDGE,"E4.sketch_text.stroke-9"),sQuery(id+"F5.wireOp",EDGE,"E4.sketch_text.stroke-10"),sQuery(id+"F5.wireOp",EDGE,"E4.sketch_text.stroke-11"),sQuery(id+"F5.wireOp",EDGE,"E4.sketch_text.stroke-12"),sQuery(id+"F5.wireOp",EDGE,"E4.sketch_text.stroke-13"),sQuery(id+"F5.wireOp",EDGE,"E4.sketch_text.stroke-14"),sQuery(id+"F5.wireOp",EDGE,"E4.sketch_text.stroke-15"),sQuery(id+"F5.wireOp",EDGE,"E4.sketch_text.stroke-16"),sQuery(id+"F5.wireOp",EDGE,"E4.sketch_text.stroke-17"),sQuery(id+"F5.wireOp",EDGE,"E4.sketch_text.stroke-18"),sQuery(id+"F5.wireOp",EDGE,"E4.sketch_text.stroke-19")])]});
            var Q7;
            Q7=makeQuery(id+"F6.opExtrude","SWEPT_BODY",BODY,{"disambiguationData":[OSD([sQuery(id+"F5.wireOp",EDGE,"E4.sketch_text.stroke-20"),sQuery(id+"F5.wireOp",EDGE,"E4.sketch_text.stroke-21"),sQuery(id+"F5.wireOp",EDGE,"E4.sketch_text.stroke-22"),sQuery(id+"F5.wireOp",EDGE,"E4.sketch_text.stroke-23")])]});
            var Q8;
            Q8=makeQuery(id+"F6.opExtrude","SWEPT_BODY",BODY,{"disambiguationData":[OSD([sQuery(id+"F5.wireOp",EDGE,"E4.sketch_text.stroke-24"),sQuery(id+"F5.wireOp",EDGE,"E4.sketch_text.stroke-25"),sQuery(id+"F5.wireOp",EDGE,"E4.sketch_text.stroke-26"),sQuery(id+"F5.wireOp",EDGE,"E4.sketch_text.stroke-27")])]});
            var Q9;
            Q9=makeQuery(id+"F6.opExtrude","SWEPT_BODY",BODY,{"disambiguationData":[OSD([sQuery(id+"F5.wireOp",EDGE,"E4.sketch_text.stroke-28"),sQuery(id+"F5.wireOp",EDGE,"E4.sketch_text.stroke-29"),sQuery(id+"F5.wireOp",EDGE,"E4.sketch_text.stroke-30"),sQuery(id+"F5.wireOp",EDGE,"E4.sketch_text.stroke-31")])]});
            var Q10;
            Q10=makeQuery(id+"F6.opExtrude","SWEPT_BODY",BODY,{"disambiguationData":[OSD([sQuery(id+"F5.wireOp",EDGE,"E4.sketch_text.stroke-32"),sQuery(id+"F5.wireOp",EDGE,"E4.sketch_text.stroke-33"),sQuery(id+"F5.wireOp",EDGE,"E4.sketch_text.stroke-34"),sQuery(id+"F5.wireOp",EDGE,"E4.sketch_text.stroke-35")])]});
            var Q11;
            Q11=makeQuery(id+"F6.opExtrude","SWEPT_BODY",BODY,{"disambiguationData":[OSD([sQuery(id+"F5.wireOp",EDGE,"E4.sketch_text.stroke-36"),sQuery(id+"F5.wireOp",EDGE,"E4.sketch_text.stroke-37"),sQuery(id+"F5.wireOp",EDGE,"E4.sketch_text.stroke-38"),sQuery(id+"F5.wireOp",EDGE,"E4.sketch_text.stroke-39"),sQuery(id+"F5.wireOp",EDGE,"E4.sketch_text.stroke-40"),sQuery(id+"F5.wireOp",EDGE,"E4.sketch_text.stroke-41"),sQuery(id+"F5.wireOp",EDGE,"E4.sketch_text.stroke-42"),sQuery(id+"F5.wireOp",EDGE,"E4.sketch_text.stroke-43"),sQuery(id+"F5.wireOp",EDGE,"E4.sketch_text.stroke-44"),sQuery(id+"F5.wireOp",EDGE,"E4.sketch_text.stroke-45"),sQuery(id+"F5.wireOp",EDGE,"E4.sketch_text.stroke-46"),sQuery(id+"F5.wireOp",EDGE,"E4.sketch_text.stroke-47"),sQuery(id+"F5.wireOp",EDGE,"E4.sketch_text.stroke-48"),sQuery(id+"F5.wireOp",EDGE,"E4.sketch_text.stroke-49"),sQuery(id+"F5.wireOp",EDGE,"E4.sketch_text.stroke-50"),sQuery(id+"F5.wireOp",EDGE,"E4.sketch_text.stroke-51"),sQuery(id+"F5.wireOp",EDGE,"E4.sketch_text.stroke-52"),sQuery(id+"F5.wireOp",EDGE,"E4.sketch_text.stroke-53"),sQuery(id+"F5.wireOp",EDGE,"E4.sketch_text.stroke-54"),sQuery(id+"F5.wireOp",EDGE,"E4.sketch_text.stroke-55"),sQuery(id+"F5.wireOp",EDGE,"E4.sketch_text.stroke-56"),sQuery(id+"F5.wireOp",EDGE,"E4.sketch_text.stroke-57"),sQuery(id+"F5.wireOp",EDGE,"E4.sketch_text.stroke-58"),sQuery(id+"F5.wireOp",EDGE,"E4.sketch_text.stroke-59"),sQuery(id+"F5.wireOp",EDGE,"E4.sketch_text.stroke-60"),sQuery(id+"F5.wireOp",EDGE,"E4.sketch_text.stroke-61"),sQuery(id+"F5.wireOp",EDGE,"E4.sketch_text.stroke-62"),sQuery(id+"F5.wireOp",EDGE,"E4.sketch_text.stroke-63"),sQuery(id+"F5.wireOp",EDGE,"E4.sketch_text.stroke-64"),sQuery(id+"F5.wireOp",EDGE,"E4.sketch_text.stroke-65"),sQuery(id+"F5.wireOp",EDGE,"E4.sketch_text.stroke-66"),sQuery(id+"F5.wireOp",EDGE,"E4.sketch_text.stroke-67")])]});
            booleanBodies(context, id + "F12", {"operationType" : BooleanOperationType.SUBTRACTION, "tools" : qUnion([Q0, Q1, Q2, Q3, Q4, Q5]), "targets" : qUnion([Q6, Q7, Q8, Q9, Q10, Q11])});
        }
        {
            var Q0;
            Q0=makeQuery(id+"F6.opExtrude","SWEPT_BODY",BODY,{"disambiguationData":[OSD([sQuery(id+"F5.wireOp",EDGE,"E5.sketch_text.stroke-0"),sQuery(id+"F5.wireOp",EDGE,"E5.sketch_text.stroke-1"),sQuery(id+"F5.wireOp",EDGE,"E5.sketch_text.stroke-2"),sQuery(id+"F5.wireOp",EDGE,"E5.sketch_text.stroke-3"),sQuery(id+"F5.wireOp",EDGE,"E5.sketch_text.stroke-4"),sQuery(id+"F5.wireOp",EDGE,"E5.sketch_text.stroke-5"),sQuery(id+"F5.wireOp",EDGE,"E5.sketch_text.stroke-6"),sQuery(id+"F5.wireOp",EDGE,"E5.sketch_text.stroke-7"),sQuery(id+"F5.wireOp",EDGE,"E5.sketch_text.stroke-8"),sQuery(id+"F5.wireOp",EDGE,"E5.sketch_text.stroke-9"),sQuery(id+"F5.wireOp",EDGE,"E5.sketch_text.stroke-10"),sQuery(id+"F5.wireOp",EDGE,"E5.sketch_text.stroke-11"),sQuery(id+"F5.wireOp",EDGE,"E5.sketch_text.stroke-12"),sQuery(id+"F5.wireOp",EDGE,"E5.sketch_text.stroke-13"),sQuery(id+"F5.wireOp",EDGE,"E5.sketch_text.stroke-14"),sQuery(id+"F5.wireOp",EDGE,"E5.sketch_text.stroke-15"),sQuery(id+"F5.wireOp",EDGE,"E5.sketch_text.stroke-16"),sQuery(id+"F5.wireOp",EDGE,"E5.sketch_text.stroke-17"),sQuery(id+"F5.wireOp",EDGE,"E5.sketch_text.stroke-18"),sQuery(id+"F5.wireOp",EDGE,"E5.sketch_text.stroke-19"),sQuery(id+"F5.wireOp",EDGE,"E5.sketch_text.stroke-20"),sQuery(id+"F5.wireOp",EDGE,"E5.sketch_text.stroke-21")])]});
            transform(context, id + "F13", {"entities" : qUnion([Q0]), "transformType" : TransformType.TRANSLATION_3D, "dx" : 1 * mm, "dy" : 0 * mm, "dz" : 0 * mm, "makeCopy" : true});
        }
        {
            var Q0;
            Q0=makeQuery(id+"F13.opPattern","COPY",BODY,{"derivedFrom":makeQuery(id+"F6.opExtrude","SWEPT_BODY",BODY,{"disambiguationData":[OSD([sQuery(id+"F5.wireOp",EDGE,"E5.sketch_text.stroke-0"),sQuery(id+"F5.wireOp",EDGE,"E5.sketch_text.stroke-1"),sQuery(id+"F5.wireOp",EDGE,"E5.sketch_text.stroke-2"),sQuery(id+"F5.wireOp",EDGE,"E5.sketch_text.stroke-3"),sQuery(id+"F5.wireOp",EDGE,"E5.sketch_text.stroke-4"),sQuery(id+"F5.wireOp",EDGE,"E5.sketch_text.stroke-5"),sQuery(id+"F5.wireOp",EDGE,"E5.sketch_text.stroke-6"),sQuery(id+"F5.wireOp",EDGE,"E5.sketch_text.stroke-7"),sQuery(id+"F5.wireOp",EDGE,"E5.sketch_text.stroke-8"),sQuery(id+"F5.wireOp",EDGE,"E5.sketch_text.stroke-9"),sQuery(id+"F5.wireOp",EDGE,"E5.sketch_text.stroke-10"),sQuery(id+"F5.wireOp",EDGE,"E5.sketch_text.stroke-11"),sQuery(id+"F5.wireOp",EDGE,"E5.sketch_text.stroke-12"),sQuery(id+"F5.wireOp",EDGE,"E5.sketch_text.stroke-13"),sQuery(id+"F5.wireOp",EDGE,"E5.sketch_text.stroke-14"),sQuery(id+"F5.wireOp",EDGE,"E5.sketch_text.stroke-15"),sQuery(id+"F5.wireOp",EDGE,"E5.sketch_text.stroke-16"),sQuery(id+"F5.wireOp",EDGE,"E5.sketch_text.stroke-17"),sQuery(id+"F5.wireOp",EDGE,"E5.sketch_text.stroke-18"),sQuery(id+"F5.wireOp",EDGE,"E5.sketch_text.stroke-19"),sQuery(id+"F5.wireOp",EDGE,"E5.sketch_text.stroke-20"),sQuery(id+"F5.wireOp",EDGE,"E5.sketch_text.stroke-21")])]}),"instanceName":"1"});
            var Q1;
            Q1=makeQuery(id+"F6.opExtrude","SWEPT_BODY",BODY,{"disambiguationData":[OSD([sQuery(id+"F5.wireOp",EDGE,"E5.sketch_text.stroke-0"),sQuery(id+"F5.wireOp",EDGE,"E5.sketch_text.stroke-1"),sQuery(id+"F5.wireOp",EDGE,"E5.sketch_text.stroke-2"),sQuery(id+"F5.wireOp",EDGE,"E5.sketch_text.stroke-3"),sQuery(id+"F5.wireOp",EDGE,"E5.sketch_text.stroke-4"),sQuery(id+"F5.wireOp",EDGE,"E5.sketch_text.stroke-5"),sQuery(id+"F5.wireOp",EDGE,"E5.sketch_text.stroke-6"),sQuery(id+"F5.wireOp",EDGE,"E5.sketch_text.stroke-7"),sQuery(id+"F5.wireOp",EDGE,"E5.sketch_text.stroke-8"),sQuery(id+"F5.wireOp",EDGE,"E5.sketch_text.stroke-9"),sQuery(id+"F5.wireOp",EDGE,"E5.sketch_text.stroke-10"),sQuery(id+"F5.wireOp",EDGE,"E5.sketch_text.stroke-11"),sQuery(id+"F5.wireOp",EDGE,"E5.sketch_text.stroke-12"),sQuery(id+"F5.wireOp",EDGE,"E5.sketch_text.stroke-13"),sQuery(id+"F5.wireOp",EDGE,"E5.sketch_text.stroke-14"),sQuery(id+"F5.wireOp",EDGE,"E5.sketch_text.stroke-15"),sQuery(id+"F5.wireOp",EDGE,"E5.sketch_text.stroke-16"),sQuery(id+"F5.wireOp",EDGE,"E5.sketch_text.stroke-17"),sQuery(id+"F5.wireOp",EDGE,"E5.sketch_text.stroke-18"),sQuery(id+"F5.wireOp",EDGE,"E5.sketch_text.stroke-19"),sQuery(id+"F5.wireOp",EDGE,"E5.sketch_text.stroke-20"),sQuery(id+"F5.wireOp",EDGE,"E5.sketch_text.stroke-21")])]});
            booleanBodies(context, id + "F14", {"operationType" : BooleanOperationType.SUBTRACTION, "tools" : qUnion([Q0]), "targets" : qUnion([Q1])});
        }
        {
            var Q0;
            Q0=makeQuery(id+"F6.opExtrude","SWEPT_BODY",BODY,{"disambiguationData":[OSD([sQuery(id+"F5.wireOp",EDGE,"E6.sketch_text.stroke-16"),sQuery(id+"F5.wireOp",EDGE,"E6.sketch_text.stroke-17"),sQuery(id+"F5.wireOp",EDGE,"E6.sketch_text.stroke-18"),sQuery(id+"F5.wireOp",EDGE,"E6.sketch_text.stroke-19"),sQuery(id+"F5.wireOp",EDGE,"E6.sketch_text.stroke-20"),sQuery(id+"F5.wireOp",EDGE,"E6.sketch_text.stroke-21"),sQuery(id+"F5.wireOp",EDGE,"E6.sketch_text.stroke-22"),sQuery(id+"F5.wireOp",EDGE,"E6.sketch_text.stroke-23"),sQuery(id+"F5.wireOp",EDGE,"E6.sketch_text.stroke-24"),sQuery(id+"F5.wireOp",EDGE,"E6.sketch_text.stroke-25"),sQuery(id+"F5.wireOp",EDGE,"E6.sketch_text.stroke-26"),sQuery(id+"F5.wireOp",EDGE,"E6.sketch_text.stroke-27"),sQuery(id+"F5.wireOp",EDGE,"E6.sketch_text.stroke-28"),sQuery(id+"F5.wireOp",EDGE,"E6.sketch_text.stroke-29"),sQuery(id+"F5.wireOp",EDGE,"E6.sketch_text.stroke-30"),sQuery(id+"F5.wireOp",EDGE,"E6.sketch_text.stroke-31"),sQuery(id+"F5.wireOp",EDGE,"E6.sketch_text.stroke-32"),sQuery(id+"F5.wireOp",EDGE,"E6.sketch_text.stroke-33"),sQuery(id+"F5.wireOp",EDGE,"E6.sketch_text.stroke-34"),sQuery(id+"F5.wireOp",EDGE,"E6.sketch_text.stroke-35"),sQuery(id+"F5.wireOp",EDGE,"E6.sketch_text.stroke-36"),sQuery(id+"F5.wireOp",EDGE,"E6.sketch_text.stroke-37")])]});
            var Q1;
            Q1=makeQuery(id+"F6.opExtrude","SWEPT_BODY",BODY,{"disambiguationData":[OSD([sQuery(id+"F5.wireOp",EDGE,"E6.sketch_text.stroke-0"),sQuery(id+"F5.wireOp",EDGE,"E6.sketch_text.stroke-1"),sQuery(id+"F5.wireOp",EDGE,"E6.sketch_text.stroke-2"),sQuery(id+"F5.wireOp",EDGE,"E6.sketch_text.stroke-3"),sQuery(id+"F5.wireOp",EDGE,"E6.sketch_text.stroke-4"),sQuery(id+"F5.wireOp",EDGE,"E6.sketch_text.stroke-5"),sQuery(id+"F5.wireOp",EDGE,"E6.sketch_text.stroke-6"),sQuery(id+"F5.wireOp",EDGE,"E6.sketch_text.stroke-7"),sQuery(id+"F5.wireOp",EDGE,"E6.sketch_text.stroke-8"),sQuery(id+"F5.wireOp",EDGE,"E6.sketch_text.stroke-9"),sQuery(id+"F5.wireOp",EDGE,"E6.sketch_text.stroke-10"),sQuery(id+"F5.wireOp",EDGE,"E6.sketch_text.stroke-11"),sQuery(id+"F5.wireOp",EDGE,"E6.sketch_text.stroke-12"),sQuery(id+"F5.wireOp",EDGE,"E6.sketch_text.stroke-13"),sQuery(id+"F5.wireOp",EDGE,"E6.sketch_text.stroke-14"),sQuery(id+"F5.wireOp",EDGE,"E6.sketch_text.stroke-15")])]});
            transform(context, id + "F15", {"entities" : qUnion([Q0, Q1]), "transformType" : TransformType.TRANSLATION_3D, "dx" : 1 * mm, "dy" : 0 * mm, "dz" : 0 * mm, "makeCopy" : true});
        }
        {
            var Q0;
            Q0=makeQuery(id+"F15.opPattern","COPY",BODY,{"derivedFrom":makeQuery(id+"F6.opExtrude","SWEPT_BODY",BODY,{"disambiguationData":[OSD([sQuery(id+"F5.wireOp",EDGE,"E6.sketch_text.stroke-16"),sQuery(id+"F5.wireOp",EDGE,"E6.sketch_text.stroke-17"),sQuery(id+"F5.wireOp",EDGE,"E6.sketch_text.stroke-18"),sQuery(id+"F5.wireOp",EDGE,"E6.sketch_text.stroke-19"),sQuery(id+"F5.wireOp",EDGE,"E6.sketch_text.stroke-20"),sQuery(id+"F5.wireOp",EDGE,"E6.sketch_text.stroke-21"),sQuery(id+"F5.wireOp",EDGE,"E6.sketch_text.stroke-22"),sQuery(id+"F5.wireOp",EDGE,"E6.sketch_text.stroke-23"),sQuery(id+"F5.wireOp",EDGE,"E6.sketch_text.stroke-24"),sQuery(id+"F5.wireOp",EDGE,"E6.sketch_text.stroke-25"),sQuery(id+"F5.wireOp",EDGE,"E6.sketch_text.stroke-26"),sQuery(id+"F5.wireOp",EDGE,"E6.sketch_text.stroke-27"),sQuery(id+"F5.wireOp",EDGE,"E6.sketch_text.stroke-28"),sQuery(id+"F5.wireOp",EDGE,"E6.sketch_text.stroke-29"),sQuery(id+"F5.wireOp",EDGE,"E6.sketch_text.stroke-30"),sQuery(id+"F5.wireOp",EDGE,"E6.sketch_text.stroke-31"),sQuery(id+"F5.wireOp",EDGE,"E6.sketch_text.stroke-32"),sQuery(id+"F5.wireOp",EDGE,"E6.sketch_text.stroke-33"),sQuery(id+"F5.wireOp",EDGE,"E6.sketch_text.stroke-34"),sQuery(id+"F5.wireOp",EDGE,"E6.sketch_text.stroke-35"),sQuery(id+"F5.wireOp",EDGE,"E6.sketch_text.stroke-36"),sQuery(id+"F5.wireOp",EDGE,"E6.sketch_text.stroke-37")])]}),"instanceName":"1"});
            var Q1;
            Q1=makeQuery(id+"F15.opPattern","COPY",BODY,{"derivedFrom":makeQuery(id+"F6.opExtrude","SWEPT_BODY",BODY,{"disambiguationData":[OSD([sQuery(id+"F5.wireOp",EDGE,"E6.sketch_text.stroke-0"),sQuery(id+"F5.wireOp",EDGE,"E6.sketch_text.stroke-1"),sQuery(id+"F5.wireOp",EDGE,"E6.sketch_text.stroke-2"),sQuery(id+"F5.wireOp",EDGE,"E6.sketch_text.stroke-3"),sQuery(id+"F5.wireOp",EDGE,"E6.sketch_text.stroke-4"),sQuery(id+"F5.wireOp",EDGE,"E6.sketch_text.stroke-5"),sQuery(id+"F5.wireOp",EDGE,"E6.sketch_text.stroke-6"),sQuery(id+"F5.wireOp",EDGE,"E6.sketch_text.stroke-7"),sQuery(id+"F5.wireOp",EDGE,"E6.sketch_text.stroke-8"),sQuery(id+"F5.wireOp",EDGE,"E6.sketch_text.stroke-9"),sQuery(id+"F5.wireOp",EDGE,"E6.sketch_text.stroke-10"),sQuery(id+"F5.wireOp",EDGE,"E6.sketch_text.stroke-11"),sQuery(id+"F5.wireOp",EDGE,"E6.sketch_text.stroke-12"),sQuery(id+"F5.wireOp",EDGE,"E6.sketch_text.stroke-13"),sQuery(id+"F5.wireOp",EDGE,"E6.sketch_text.stroke-14"),sQuery(id+"F5.wireOp",EDGE,"E6.sketch_text.stroke-15")])]}),"instanceName":"1"});
            var Q2;
            Q2=makeQuery(id+"F6.opExtrude","SWEPT_BODY",BODY,{"disambiguationData":[OSD([sQuery(id+"F5.wireOp",EDGE,"E6.sketch_text.stroke-16"),sQuery(id+"F5.wireOp",EDGE,"E6.sketch_text.stroke-17"),sQuery(id+"F5.wireOp",EDGE,"E6.sketch_text.stroke-18"),sQuery(id+"F5.wireOp",EDGE,"E6.sketch_text.stroke-19"),sQuery(id+"F5.wireOp",EDGE,"E6.sketch_text.stroke-20"),sQuery(id+"F5.wireOp",EDGE,"E6.sketch_text.stroke-21"),sQuery(id+"F5.wireOp",EDGE,"E6.sketch_text.stroke-22"),sQuery(id+"F5.wireOp",EDGE,"E6.sketch_text.stroke-23"),sQuery(id+"F5.wireOp",EDGE,"E6.sketch_text.stroke-24"),sQuery(id+"F5.wireOp",EDGE,"E6.sketch_text.stroke-25"),sQuery(id+"F5.wireOp",EDGE,"E6.sketch_text.stroke-26"),sQuery(id+"F5.wireOp",EDGE,"E6.sketch_text.stroke-27"),sQuery(id+"F5.wireOp",EDGE,"E6.sketch_text.stroke-28"),sQuery(id+"F5.wireOp",EDGE,"E6.sketch_text.stroke-29"),sQuery(id+"F5.wireOp",EDGE,"E6.sketch_text.stroke-30"),sQuery(id+"F5.wireOp",EDGE,"E6.sketch_text.stroke-31"),sQuery(id+"F5.wireOp",EDGE,"E6.sketch_text.stroke-32"),sQuery(id+"F5.wireOp",EDGE,"E6.sketch_text.stroke-33"),sQuery(id+"F5.wireOp",EDGE,"E6.sketch_text.stroke-34"),sQuery(id+"F5.wireOp",EDGE,"E6.sketch_text.stroke-35"),sQuery(id+"F5.wireOp",EDGE,"E6.sketch_text.stroke-36"),sQuery(id+"F5.wireOp",EDGE,"E6.sketch_text.stroke-37")])]});
            var Q3;
            Q3=makeQuery(id+"F6.opExtrude","SWEPT_BODY",BODY,{"disambiguationData":[OSD([sQuery(id+"F5.wireOp",EDGE,"E6.sketch_text.stroke-0"),sQuery(id+"F5.wireOp",EDGE,"E6.sketch_text.stroke-1"),sQuery(id+"F5.wireOp",EDGE,"E6.sketch_text.stroke-2"),sQuery(id+"F5.wireOp",EDGE,"E6.sketch_text.stroke-3"),sQuery(id+"F5.wireOp",EDGE,"E6.sketch_text.stroke-4"),sQuery(id+"F5.wireOp",EDGE,"E6.sketch_text.stroke-5"),sQuery(id+"F5.wireOp",EDGE,"E6.sketch_text.stroke-6"),sQuery(id+"F5.wireOp",EDGE,"E6.sketch_text.stroke-7"),sQuery(id+"F5.wireOp",EDGE,"E6.sketch_text.stroke-8"),sQuery(id+"F5.wireOp",EDGE,"E6.sketch_text.stroke-9"),sQuery(id+"F5.wireOp",EDGE,"E6.sketch_text.stroke-10"),sQuery(id+"F5.wireOp",EDGE,"E6.sketch_text.stroke-11"),sQuery(id+"F5.wireOp",EDGE,"E6.sketch_text.stroke-12"),sQuery(id+"F5.wireOp",EDGE,"E6.sketch_text.stroke-13"),sQuery(id+"F5.wireOp",EDGE,"E6.sketch_text.stroke-14"),sQuery(id+"F5.wireOp",EDGE,"E6.sketch_text.stroke-15")])]});
            booleanBodies(context, id + "F16", {"operationType" : BooleanOperationType.SUBTRACTION, "tools" : qUnion([Q0, Q1]), "targets" : qUnion([Q2, Q3])});
        }
    });
